# Revit family: Planet-Wattohm boites de sol version standard
name_source: partatom
category: Installations électriques
units: mm (PartAtom-declared; Revit-internal decimal feet)

## family parameters
Conserver l'orientation des annotations = Non
Cote de connecteur circulaire = Utiliser le diamètre
Couper avec des vides une fois chargée = Non
Hôte = Face
Partagée = Non
Point de calcul de pièce = Non
Type d'élément = Normal

## types (9) — shared parameters
00 = Reservation boitier : 00
000000 = Accessoire : None
01 = Reservation boitier : 01
02 = Reservation boitier : 02
26 = Reservation boitier : 26
27 = Reservation boitier : 27
28 = Reservation boitier : 28
80 = Reservation boitier : 80
90 = Reservation boitier : 90
91 = Reservation boitier : 91
92 = Reservation boitier : 92
Auto = Type de sol utilisé : Auto ajustable
Brass = Finition : Laiton
Fabricant = LEGRAND
Inox = Finition : Acier inoxydable
PW-28500 = Boitier d'encastrement : PW-28500
PW-28501 = Accessoire : PW-28501
PW-28502 = Accessoire : PW-28502
PW-28503 = Accessoire : PW-28503
PW-28510 = Accessoire : PW-28510 + PW-28511
PW-28510-2 = Accessoire : PW-28510 + (2xPW-28511)
PW-28512 = Boitier d'encastrement : PW-28512
PW-28514 = Accessoire : PW-28514
PW-28516 = Accessoire : PW-28516
PW-28518 = Boitier d'encastrement : PW-28518
PW-28524 = Boitier d'encastrement : PW-28524
PW-28528 = Accessoire : PW-28528
PW-28710 = Plaque finition : PW-28710
PW-28711 = Plaque finition : PW-28711
PW-28712 = Couvercle : PW-28712
PW-28713 = Plaque finition : PW-28713
PW-28718 = Couvercle : PW-28718
PW-28720 = Plaque finition : PW-28720
PW-28721 = Plaque finition : PW-28721
PW-28723 = Plaque finition : PW-28723
PW-28724 = Couvercle : PW-28724
PW-28730 = Plaque finition : PW-28730
PW-28731 = Plaque finition : PW-28731
PW-28733 = Plaque finition : PW-28733
PW-28741 = Couvercle : PW-28741
PW-28743 = Couvercle : PW-28743
PW-28751 = Couvercle : PW-28751
PW-28753 = Couvercle : PW-28753
PW-28761 = Couvercle : PW-28761
PW-28763 = Couvercle : PW-28763
Plastic = Finition : Gris RAL 7031
StdB125 = Type de sol utilisé : Plancher béton inférieur 125 mm
StdB170 = Type de sol utilisé : Plancher béton entre 125 mm et 170 mm
StdB250 = Type de sol utilisé : Plancher béton entre 170 mm et 250 mm
StdT = Type de sol utilisé : Plancher technique
zero-valued in all types: Elévation par défaut

## per-type parameters (varying)
| type | Description | Support | Support appareillage | Supports |
| 8 modules 2x4 | Boite de sol universelle standard 8 modules vertical | 23 | Support appareillage : PW-28622 | PW-28622 |
| 12 modules 2x6 | Boite de sol universelle standard 12 modules vertical | 24 | Support appareillage : PW-28628 | PW-28628 |
| 16 modules 2x8 | Boite de sol universelle standard 16 modules vertical | 25 | Support appareillage : PW-28624 | PW-28624 |
| 12 modules 3x4 | Boite de sol universelle standard 12 modules horizontal ajustable | 20 | Support appareillage : PW-28604 | PW-28604 |
| 18 modules 3x6 | Boite de sol universelle standard 18 modules horizontal ajustable | 21 | Support appareillage : PW-28606 | PW-28606 |
| 24 modules 3x8 | Boite de sol universelle standard 24 modules horizontal ajustable | 22 | Support appareillage : PW-28608 | PW-28608 |
| Trappe de visite 8-12 modules | Trappe de visite couvercle standard 8/12 modules | 39 | Support appareillage : PW-28529 | PW-28529 |
| Trappe de visite 12-18 modules | Trappe de visite couvercle standard 12/18 modules | 40 | Support appareillage : PW-28530 | PW-28530 |
| Trappe de visite 16-24 modules | Trappe de visite couvercle standard 16/24 modules | 41 | Support appareillage : PW-28531 | PW-28531 |
